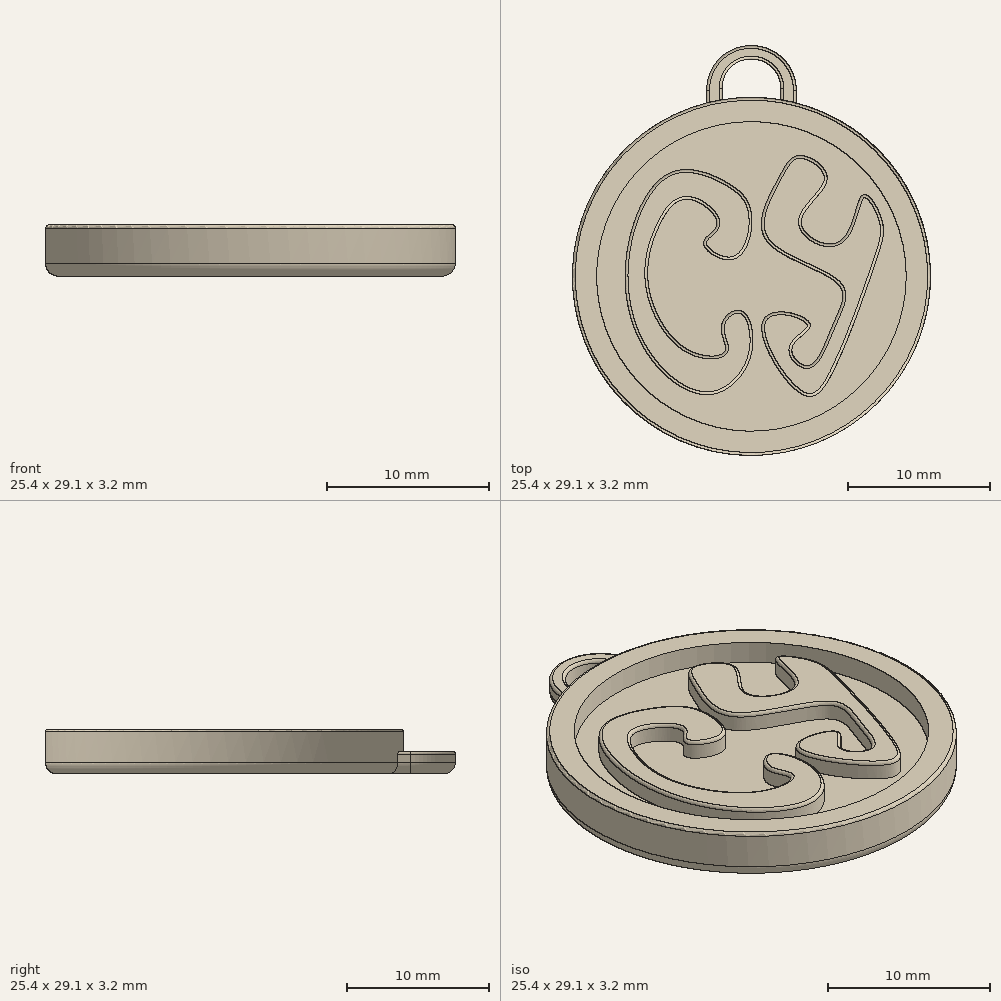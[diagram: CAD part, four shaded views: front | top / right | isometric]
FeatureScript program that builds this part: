
annotation { "Feature Type Name" : "Feature", "Feature Type Description" : "" }
export const myFeature = defineFeature(function(context is Context, id is Id, definition is map)
    precondition{}
    {
        {
            var Q0;
            Q0=qCreatedBy(makeId("Top.planeOp"),FACE);
            var sketch = newSketch(context, id + "F0", { "sketchPlane" : qUnion([Q0])});
            skCircle(sketch, "E0", {"center": v(0, 0) * mm, "radius": 12.7 * mm});
            skSolve(sketch);
        }
        {
            var Q0;
            Q0=makeQuery(id+"F0.imprint","IMPRINT",FACE,{"disambiguationData":[TD([[makeQuery(id+"F0.imprint","IMPRINT",EDGE,{"derivedFrom":sQuery(id+"F0.wireOp",EDGE,"E0")}),1.0]])]});
            extrude(context, id + "F1", {"entities" : qUnion([Q0]), "depth" : 3.17 * mm});
        }
        {
            var Q0;
            Q0=makeQuery(id+"F1.opExtrude","CAP_FACE",FACE,{"disambiguationData":[OSD([sQuery(id+"F0.wireOp",EDGE,"E0")])],"isStart":false});
            var sketch = newSketch(context, id + "F2", { "sketchPlane" : qUnion([Q0])});
            skCircle(sketch, "E1", {"center": v(0, 0) * mm, "radius": 10.98 * mm});
            skSolve(sketch);
        }
        {
            var Q0;
            Q0=makeQuery(id+"F2.imprint","IMPRINT",FACE,{"disambiguationData":[TD([[makeQuery(id+"F2.imprint","IMPRINT",EDGE,{"derivedFrom":sQuery(id+"F2.wireOp",EDGE,"E1")}),1.0]])]});
            extrude(context, id + "F3", {"entities" : qUnion([Q0]), "operationType" : NewBodyOperationType.REMOVE, "oppositeDirection" : true, "depth" : 1.42 * mm});
        }
        {
            var Q0;
            Q0=qCreatedBy(makeId("Top.planeOp"),FACE);
            var sketch = newSketch(context, id + "F4", { "sketchPlane" : qUnion([Q0])});
            skLineSegment(sketch, "E2.top", {"start": v(0, 16.38) * mm, "end": v(0, 16.38) * mm});
            skLineSegment(sketch, "E2.left", {"start": v(-3.18, 12.3) * mm, "end": v(-3.18, 13.2) * mm});
            skLineSegment(sketch, "E2.right", {"start": v(3.18, 12.3) * mm, "end": v(3.18, 13.2) * mm});
            skArc(sketch, "E3", {"start": v(2.08, 13.34) * mm, "mid": v(0, 15.42) * mm, "end": v(-2.08, 13.34) * mm});
            skLineSegment(sketch, "E4", {"start": v(-2.08, 13.34) * mm, "end": v(-2.08, 12.53) * mm});
            skLineSegment(sketch, "E5", {"start": v(2.08, 13.34) * mm, "end": v(2.08, 12.53) * mm});
            skPoint(sketch, "E6.visualSharp", {"position": v(-3.18, 16.38) * mm});
            skArc(sketch, "E6.filletArc", {"start": v(0, 16.38) * mm, "mid": v(-2.25, 15.45) * mm, "end": v(-3.17, 13.2) * mm});
            skPoint(sketch, "E7.visualSharp", {"position": v(3.17, 16.38) * mm});
            skArc(sketch, "E7.filletArc", {"start": v(3.18, 13.2) * mm, "mid": v(2.25, 15.45) * mm, "end": v(0, 16.38) * mm});
            skArc(sketch, "E8.0", {"start": v(3.18, 12.3) * mm, "mid": v(0, 12.7) * mm, "end": v(-3.17, 12.3) * mm});
            skPoint(sketch, "E9.orphan", {"position": v(-2.08, 9.87) * mm});
            skPoint(sketch, "E10.orphan", {"position": v(2.08, 9.87) * mm});
            skSolve(sketch);
        }
        {
            var Q0;
            {var subQ2=sQuery(id+"F4.wireOp",EDGE,"E2.left");Q0=makeQuery(id+"F4.imprint","IMPRINT",FACE,{"disambiguationData":[TD([[makeQuery(id+"F4.imprint","IMPRINT",EDGE,{"derivedFrom":subQ2}),-1.0]])]});}
            extrude(context, id + "F5", {"entities" : qUnion([Q0]), "operationType" : NewBodyOperationType.ADD, "depth" : 1.59 * mm});
        }
        {
            var Q0;
            {var subQ1=sQuery(id+"F4.wireOp",EDGE,"E2.left");var subQ2=sQuery(id+"F0.wireOp",EDGE,"E0");Q0=makeQuery(id+"F5.boolean.opBoolean","SPLIT",EDGE,{"disambiguationData":[TD([makeQuery(id+"F5.opExtrude","SWEPT_FACE",FACE,{"disambiguationData":[OSD([subQ1])]})])],"derivedFrom":makeQuery(id+"F1.opExtrude","CAP_EDGE",EDGE,{"disambiguationData":[OSD([subQ2])],"isStart":true})});}
            var Q1;
            Q1=makeQuery(id+"F5.opExtrude","CAP_EDGE",EDGE,{"disambiguationData":[OSD([sQuery(id+"F4.wireOp",EDGE,"E6.filletArc"),sQuery(id+"F4.wireOp",EDGE,"E7.filletArc")])],"isStart":true});
            var Q2;
            Q2=makeQuery(id+"F5.opExtrude","CAP_EDGE",EDGE,{"disambiguationData":[OSD([sQuery(id+"F4.wireOp",EDGE,"E2.right")])],"isStart":true});
            fillet(context, id + "F6", {"entities" : qUnion([Q0, Q1, Q2]), "radius" : 0.8 * mm, "tangentPropagation" : true, "allowEdgeOverflow" : false});
        }
        {
            var Q0;
            Q0=makeQuery(id+"F3.boolean.opBoolean","COPY",FACE,{"derivedFrom":makeQuery(id+"F3.opExtrude","CAP_FACE",FACE,{"disambiguationData":[OSD([sQuery(id+"F2.wireOp",EDGE,"E1")])],"isStart":false})});
            var sketch = newSketch(context, id + "F7", { "sketchPlane" : qUnion([Q0])});
            skFitSpline(sketch, "E11", {"points": [v(-1.63, 6.6) * mm, v(-5.58, 7.41) * mm, v(-8.74, 2.27) * mm, v(-7.6, -5.12) * mm, v(-2.99, -8.39) * mm, v(0, -5.5) * mm, v(-0.79, -2.41) * mm, v(-2.14, -3.58) * mm, v(-1.86, -5.29) * mm, v(-4.34, -5.29) * mm, v(-7.27, -0.83) * mm, v(-6.54, 3.56) * mm, v(-4.47, 5.46) * mm, v(-2.44, 3.67) * mm, v(-3.4, 2.36) * mm, v(-1.25, 1.21) * mm, v(0, 4.45) * mm, v(-1.63, 6.6) * mm]});
            skFitSpline(sketch, "E12", {"points": [v(1.92, 6.95) * mm, v(0.99, 2.65) * mm, v(6.24, -0.65) * mm, v(5.73, -3.53) * mm, v(4, -6.32) * mm, v(2.87, -5.12) * mm, v(4.17, -3.54) * mm, v(2.37, -2.52) * mm, v(0.73, -3.55) * mm, v(3.78, -8.44) * mm, v(5.86, -6.65) * mm, v(8.93, 1.34) * mm, v(9.22, 4.12) * mm, v(7.92, 5.78) * mm, v(6.25, 2.48) * mm, v(3.54, 3.76) * mm, v(5.37, 6.89) * mm, v(3.5, 8.57) * mm, v(1.92, 6.95) * mm]});
            skSolve(sketch);
        }
        {
            var Q0;
            Q0=makeQuery(id+"F7.imprint","IMPRINT",FACE,{"disambiguationData":[TD([[makeQuery(id+"F7.imprint","IMPRINT",EDGE,{"derivedFrom":sQuery(id+"F7.wireOp",EDGE,"E12")}),1.0]])]});
            var Q1;
            Q1=makeQuery(id+"F7.imprint","IMPRINT",FACE,{"disambiguationData":[TD([[makeQuery(id+"F7.imprint","IMPRINT",EDGE,{"derivedFrom":sQuery(id+"F7.wireOp",EDGE,"E11")}),1.0]])]});
            extrude(context, id + "F8", {"entities" : qUnion([Q0, Q1]), "operationType" : NewBodyOperationType.ADD, "depth" : 1.17 * mm});
        }
        {
            var Q0;
            Q0=makeQuery(id+"F8.opExtrude","CAP_EDGE",EDGE,{"disambiguationData":[OSD([sQuery(id+"F7.wireOp",EDGE,"E11")])],"isStart":false});
            var Q1;
            Q1=makeQuery(id+"F8.opExtrude","CAP_EDGE",EDGE,{"disambiguationData":[OSD([sQuery(id+"F7.wireOp",EDGE,"E12")])],"isStart":false});
            fillet(context, id + "F9", {"entities" : qUnion([Q0, Q1]), "radius" : 0.2 * mm, "tangentPropagation" : true, "allowEdgeOverflow" : false});
        }
        {
            var Q0;
            Q0=makeQuery(id+"F3.boolean.opBoolean","COPY",EDGE,{"derivedFrom":makeQuery(id+"F3.opExtrude","CAP_EDGE",EDGE,{"disambiguationData":[OSD([sQuery(id+"F2.wireOp",EDGE,"E1")])],"isStart":true})});
            var Q1;
            Q1=makeQuery(id+"F1.opExtrude","CAP_EDGE",EDGE,{"disambiguationData":[OSD([sQuery(id+"F0.wireOp",EDGE,"E0")])],"isStart":false});
            var Q2;
            Q2=makeQuery(id+"F5.opExtrude","CAP_EDGE",EDGE,{"disambiguationData":[OSD([sQuery(id+"F4.wireOp",EDGE,"E6.filletArc"),sQuery(id+"F4.wireOp",EDGE,"E7.filletArc")])],"isStart":false});
            var Q3;
            Q3=makeQuery(id+"F5.opExtrude","CAP_EDGE",EDGE,{"disambiguationData":[OSD([sQuery(id+"F4.wireOp",EDGE,"E2.left")])],"isStart":false});
            var Q4;
            Q4=makeQuery(id+"F5.opExtrude","CAP_EDGE",EDGE,{"disambiguationData":[OSD([sQuery(id+"F4.wireOp",EDGE,"E3")])],"isStart":false});
            var Q5;
            Q5=makeQuery(id+"F5.opExtrude","SWEPT_EDGE",EDGE,{"disambiguationData":[OSD([sQuery(id+"F4.wireOp",EDGE,"E5"),sQuery(id+"F4.wireOp",EDGE,"E8.0")])]});
            var Q6;
            Q6=makeQuery(id+"F5.opExtrude","SWEPT_EDGE",EDGE,{"disambiguationData":[OSD([sQuery(id+"F4.wireOp",EDGE,"E4"),sQuery(id+"F4.wireOp",EDGE,"E8.0")])]});
            fillet(context, id + "F10", {"entities" : qUnion([Q0, Q1, Q2, Q3, Q4, Q5, Q6]), "radius" : 0.2 * mm, "tangentPropagation" : true, "allowEdgeOverflow" : false});
        }
    });
